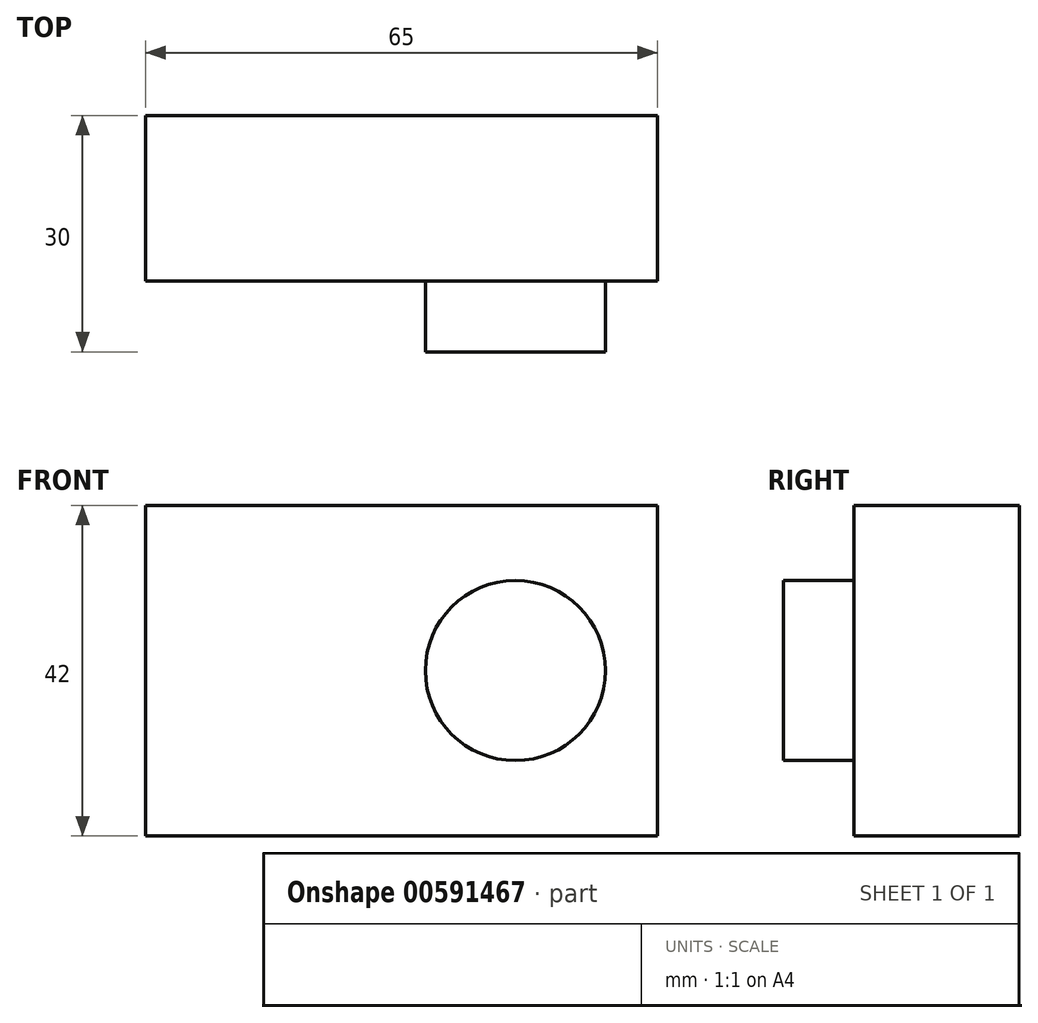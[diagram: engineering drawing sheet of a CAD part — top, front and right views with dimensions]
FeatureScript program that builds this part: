
annotation { "Feature Type Name" : "Feature", "Feature Type Description" : "" }
export const myFeature = defineFeature(function(context is Context, id is Id, definition is map)
    precondition{}
    {
        {
            var Q0;
            Q0=qCreatedBy(makeId("Top.planeOp"),FACE);
            var sketch = newSketch(context, id + "F0", { "sketchPlane" : qUnion([Q0])});
            skLineSegment(sketch, "E0.bottom", {"start": v(32.5, 10.5) * mm, "end": v(-32.5, 10.5) * mm});
            skLineSegment(sketch, "E0.top", {"start": v(32.5, -10.5) * mm, "end": v(-32.5, -10.5) * mm});
            skLineSegment(sketch, "E0.left", {"start": v(32.5, 10.5) * mm, "end": v(32.5, -10.5) * mm});
            skLineSegment(sketch, "E0.right", {"start": v(-32.5, 10.5) * mm, "end": v(-32.5, -10.5) * mm});
            skPoint(sketch, "E0.middle", {"position": v(0, 0) * mm});
            skSolve(sketch);
        }
        {
            var Q0;
            Q0=makeQuery(id+"F0.imprint","IMPRINT",FACE,{"disambiguationData":[TD([[makeQuery(id+"F0.imprint","IMPRINT",EDGE,{"derivedFrom":sQuery(id+"F0.wireOp",EDGE,"E0.bottom")}),1.0]])]});
            extrude(context, id + "F1", {"entities" : qUnion([Q0]), "depth" : 42 * mm, "offsetDistance" : 25 * mm});
        }
        {
            var Q0;
            Q0=makeQuery(id+"F1.opExtrude","SWEPT_FACE",FACE,{"disambiguationData":[OSD([sQuery(id+"F0.wireOp",EDGE,"E0.top")])]});
            var sketch = newSketch(context, id + "F2", { "sketchPlane" : qUnion([Q0])});
            skCircle(sketch, "E1", {"center": v(14.47, 21) * mm, "radius": 11.44 * mm});
            skSolve(sketch);
        }
        {
            var Q0;
            Q0=makeQuery(id+"F2.imprint","IMPRINT",FACE,{"disambiguationData":[TD([[makeQuery(id+"F2.imprint","IMPRINT",EDGE,{"derivedFrom":sQuery(id+"F2.wireOp",EDGE,"E1")}),1.0]])]});
            extrude(context, id + "F3", {"entities" : qUnion([Q0]), "operationType" : NewBodyOperationType.ADD, "depth" : 9 * mm, "offsetDistance" : 25 * mm});
        }
    });
